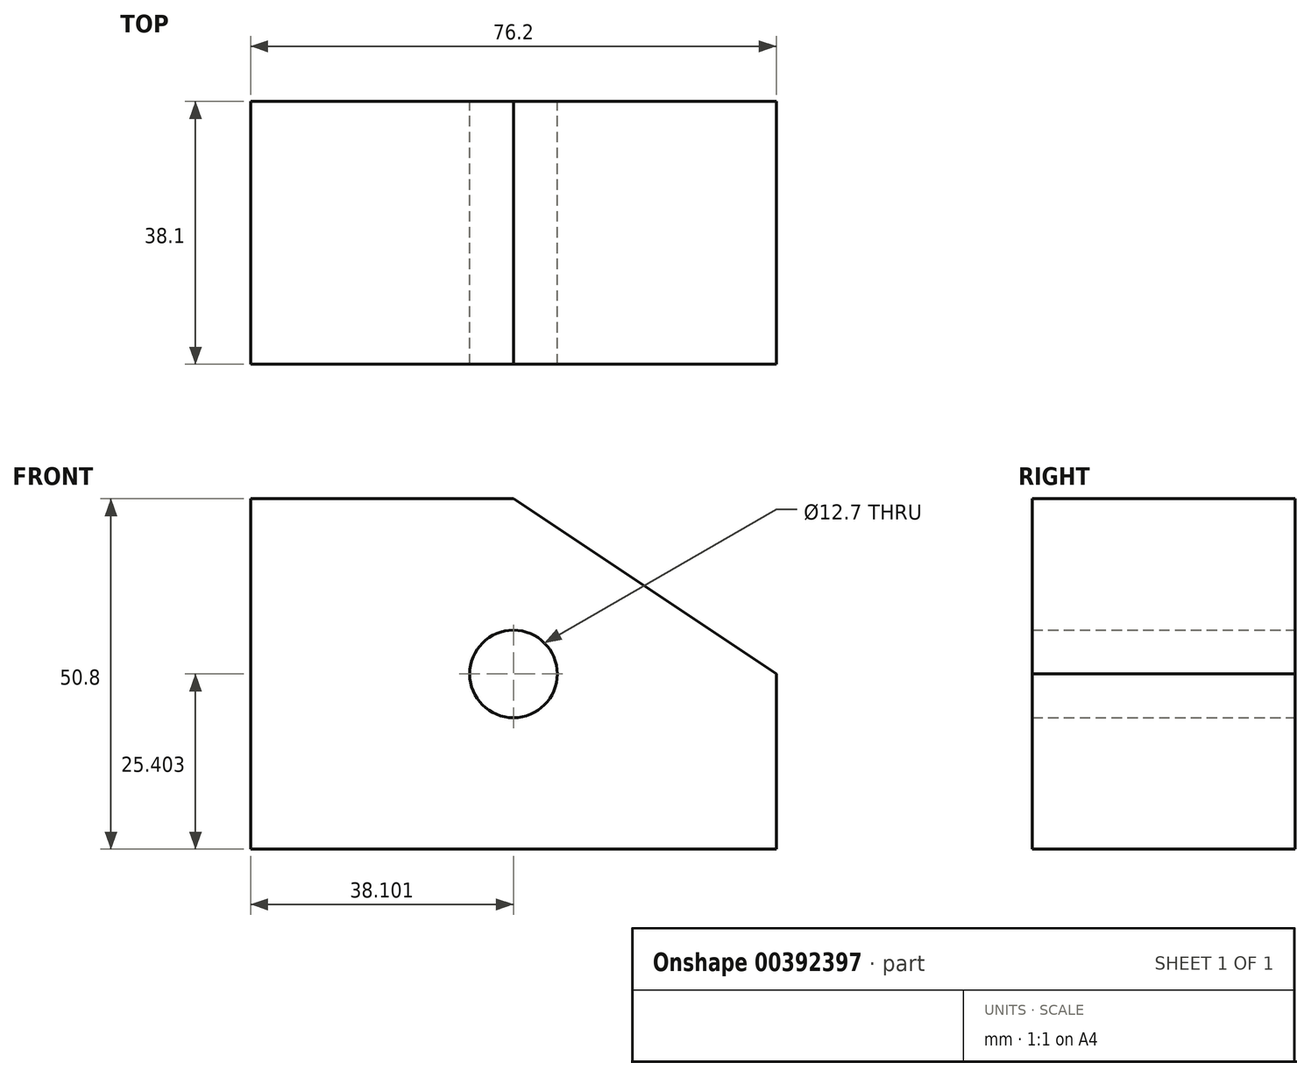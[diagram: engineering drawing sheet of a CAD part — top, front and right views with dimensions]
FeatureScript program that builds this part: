
annotation { "Feature Type Name" : "Feature", "Feature Type Description" : "" }
export const myFeature = defineFeature(function(context is Context, id is Id, definition is map)
    precondition{}
    {
        {
            var Q0;
            Q0=qCreatedBy(makeId("Front.planeOp"),FACE);
            var sketch = newSketch(context, id + "F0", { "sketchPlane" : qUnion([Q0])});
            skLineSegment(sketch, "E0", {"start": v(-42.69, 47.58) * mm, "end": v(-42.69, -3.22) * mm});
            skLineSegment(sketch, "E1", {"start": v(-42.69, 47.58) * mm, "end": v(-4.59, 47.58) * mm});
            skLineSegment(sketch, "E2", {"start": v(-42.69, -3.22) * mm, "end": v(33.51, -3.22) * mm});
            skLineSegment(sketch, "E3", {"start": v(33.51, -3.22) * mm, "end": v(33.51, 22.18) * mm});
            skLineSegment(sketch, "E4", {"start": v(-4.59, 47.58) * mm, "end": v(33.51, 22.18) * mm});
            skCircle(sketch, "E5", {"center": v(-4.59, 22.18) * mm, "radius": 6.35 * mm});
            skSolve(sketch);
        }
        {
            var Q0;
            Q0=makeQuery(id+"F0.imprint","IMPRINT",FACE,{"disambiguationData":[TD([[makeQuery(id+"F0.imprint","IMPRINT",EDGE,{"derivedFrom":sQuery(id+"F0.wireOp",EDGE,"E0")}),1.0]])]});
            extrude(context, id + "F1", {"entities" : qUnion([Q0]), "depth" : 38.1 * mm});
        }
    });
